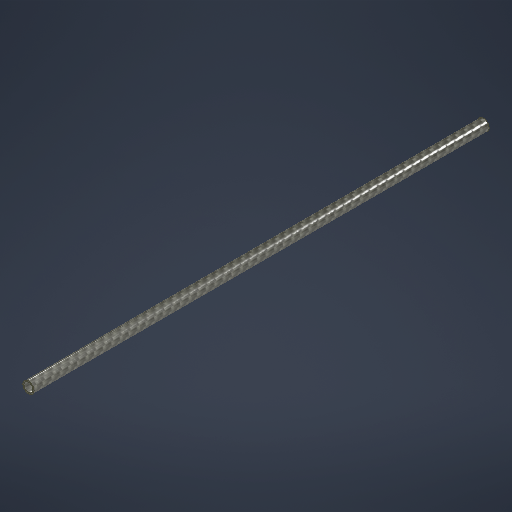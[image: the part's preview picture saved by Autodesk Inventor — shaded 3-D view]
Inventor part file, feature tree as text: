
AUTODESK INVENTOR PART (.ipt)
format: ipt  version: 2025 (Build 290162010, 162A)  size: 216,064 bytes
history: native  units: mm
features: extrude x1
ambient origin geometry x8: Origin, YZ Plane, XZ Plane, XY Plane, X Axis, Y Axis, Z Axis, Center Point
bodies: Solid1 (feature_tree)
feature tree (1):
  extrude  "Extrusion1"  Depth=10.0mm
